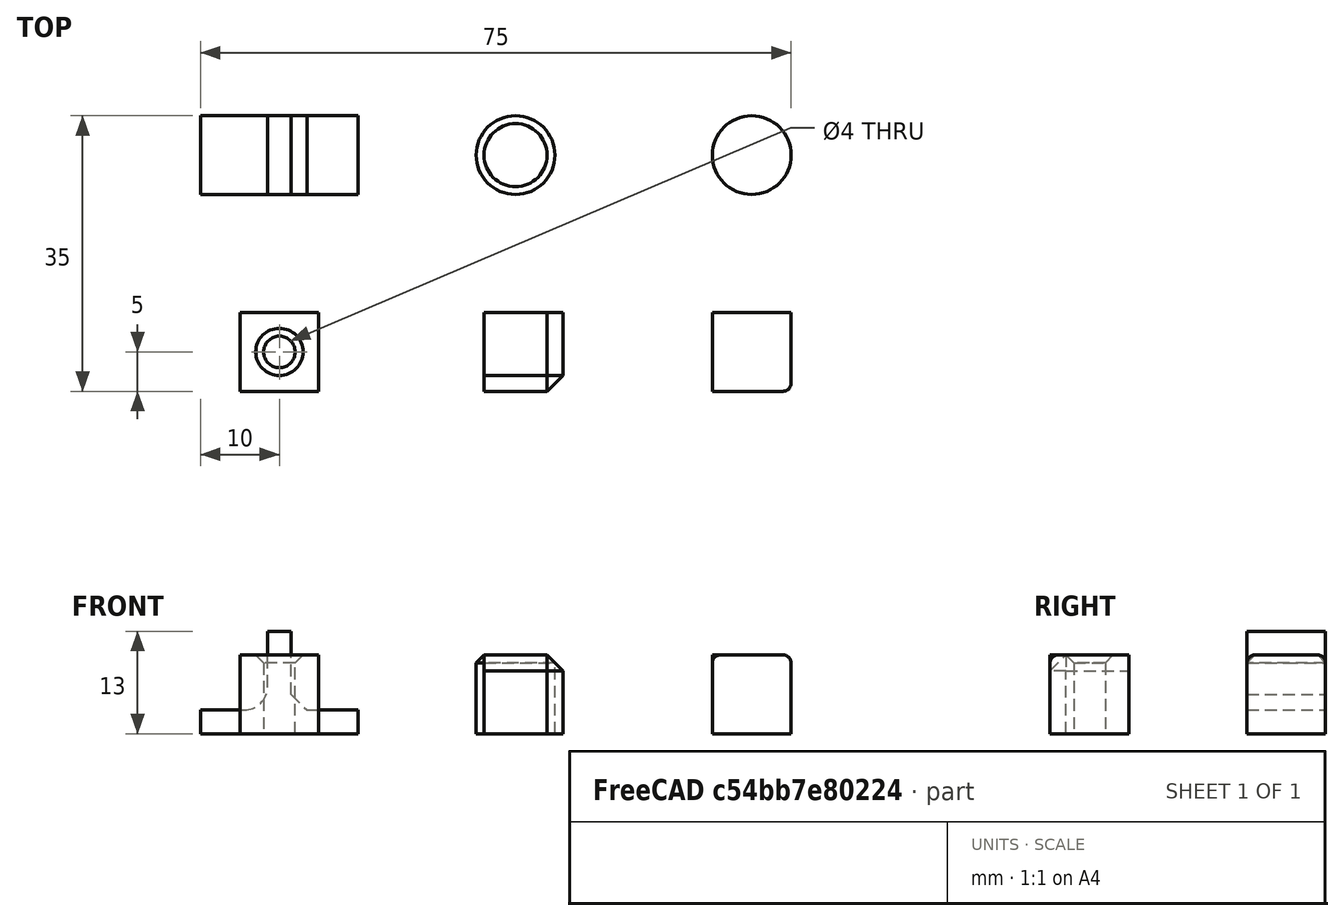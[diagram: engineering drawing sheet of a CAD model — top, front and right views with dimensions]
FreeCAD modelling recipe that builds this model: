
FCSTD DOCUMENT  (FreeCAD 1.0R39319 (Git))
Label: ojt1_t12p01_roundings_chamfers_reinforcements
License: All rights reserved
LicenseURL: https://en.wikipedia.org/wiki/All_rights_reserved
objects: Part::Box×5, Part::Chamfer×4, Part::Fillet×3, Part::Cylinder×3, Part::Cut×1, Part::MultiFuse×1
note: 17 computed .brp shape members not serialized (recipe doc carries the construction recipe); baked Part::Feature solids carry a one-line shape summary decoded from their .brp

FEATURE [Part::Box] Box  label="Cub"
  AttacherType = Attacher::AttachEngine3D
  Height = 10
  Length = 10
  Width = 10
FEATURE [Part::Fillet] Fillet
  Base = -> Box
  EdgeLinks = -> Box [Edge5,Edge6,Edge10]
  Edges = 3 edges r=1: [Edge5,Edge6,Edge10]
  Placement = pos=(5,0,0) rot=(0,0,1;0rad)
FEATURE [Part::Box] Box001  label="Cub001"
  AttacherType = Attacher::AttachEngine3D
  Height = 10
  Length = 10
  Placement = pos=(-20,0,0) rot=(0,0,1;0rad)
  Width = 10
FEATURE [Part::Chamfer] Chamfer
  Base = -> Box001
  EdgeLinks = -> Box001 [Edge5,Edge6,Edge10]
  Edges = 3 edges r=2: [Edge5,Edge6,Edge10]
  Placement = pos=(-4,0,0) rot=(0,0,1;0rad)
FEATURE [Part::Box] Box002  label="Cub002"
  AttacherType = Attacher::AttachEngine3D
  Height = 10
  Length = 10
  Placement = pos=(-40,0,0) rot=(0,0,1;0rad)
  Width = 10
FEATURE [Part::Cylinder] Cylinder  label="Cilindre"
  Angle = 360
  AttacherType = Attacher::AttachEngine3D
  FirstAngle = 0
  Height = 12
  Placement = pos=(-35,5,-1) rot=(0,0,1;0rad)
  Radius = 2
  SecondAngle = 0
FEATURE [Part::Cut] Cut
  Base = -> Box002
  Refine = true
  Tool = -> Cylinder
FEATURE [Part::Chamfer] Chamfer001
  Base = -> Cut
  EdgeLinks = -> Cut [Edge10]
  Edges = 1 edges r=1: [Edge10]
  Placement = pos=(-15,0,0) rot=(0,0,1;0rad)
FEATURE [Part::Cylinder] Cylinder001  label="Cilindre001"
  Angle = 360
  AttacherType = Attacher::AttachEngine3D
  FirstAngle = 0
  Height = 10
  Placement = pos=(5,30,0) rot=(0,0,1;0rad)
  Radius = 5
  SecondAngle = 0
FEATURE [Part::Fillet] Fillet001
  Base = -> Cylinder001
  EdgeLinks = -> Cylinder001 [Edge3]
  Edges = 1 edges r=1: [Edge3]
  Placement = pos=(5,0,0) rot=(0,0,1;0rad)
FEATURE [Part::Cylinder] Cylinder002  label="Cilindre002"
  Angle = 360
  AttacherType = Attacher::AttachEngine3D
  FirstAngle = 0
  Height = 10
  Placement = pos=(-20,30,0) rot=(0,0,1;0rad)
  Radius = 5
  SecondAngle = 0
FEATURE [Part::Chamfer] Chamfer002
  Base = -> Cylinder002
  EdgeLinks = -> Cylinder002 [Edge3]
  Edges = 1 edges r=1: [Edge3]
FEATURE [Part::Box] Box003  label="Cub003"
  AttacherType = Attacher::AttachEngine3D
  Height = 3
  Length = 20
  Placement = pos=(-60,25,0) rot=(0,0,1;0rad)
  Width = 10
FEATURE [Part::Box] Box004  label="Cub004"
  AttacherType = Attacher::AttachEngine3D
  Height = 13
  Length = 3
  Placement = pos=(-51.5,25,0) rot=(0,0,1;0rad)
  Width = 10
FEATURE [Part::MultiFuse] Fusion
  Refine = true
  Shapes = -> [Box003,Box004]
FEATURE [Part::Chamfer] Chamfer003
  Base = -> Fusion
  EdgeLinks = -> Fusion [Edge16]
  Edges = 1 edges r=2: [Edge16]
FEATURE [Part::Fillet] Fillet002
  Base = -> Chamfer003
  EdgeLinks = -> Chamfer003 [Edge27]
  Edges = 1 edges r=3: [Edge27]
